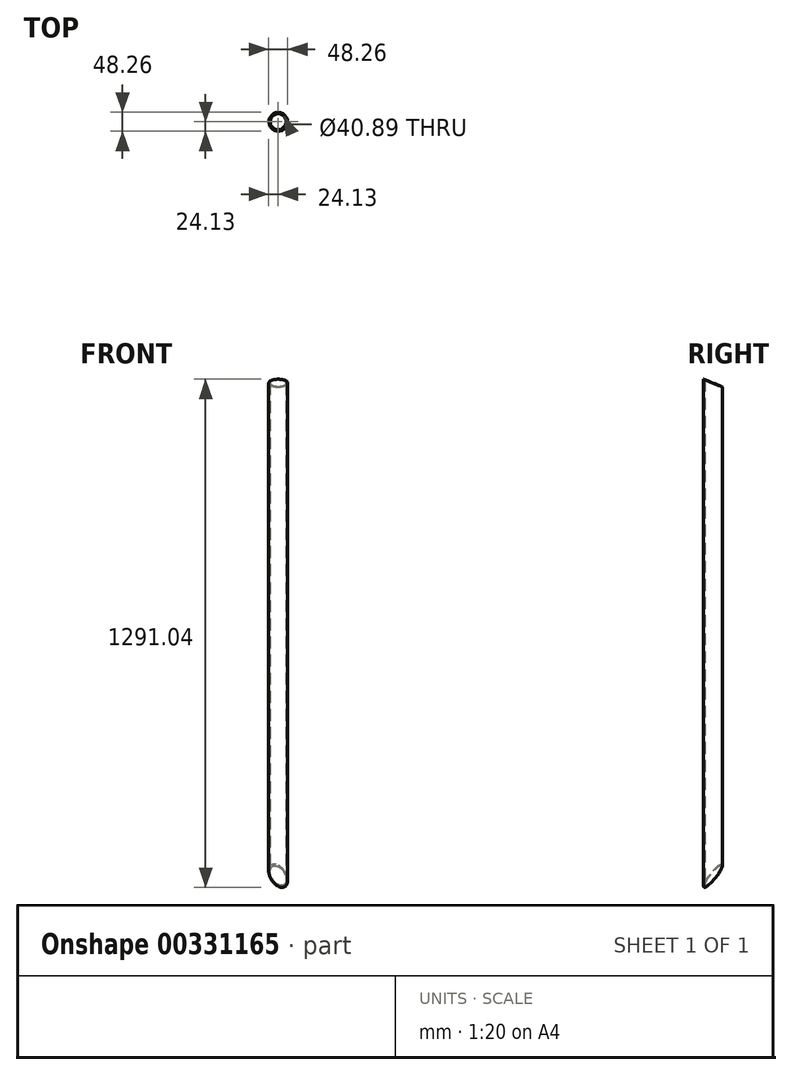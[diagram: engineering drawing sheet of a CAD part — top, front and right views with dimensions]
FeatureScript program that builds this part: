
annotation { "Feature Type Name" : "Feature", "Feature Type Description" : "" }
export const myFeature = defineFeature(function(context is Context, id is Id, definition is map)
    precondition{}
    {
        {
            var Q0;
            Q0=qCreatedBy(makeId("Top.planeOp"),FACE);
            var sketch = newSketch(context, id + "F0", { "sketchPlane" : qUnion([Q0])});
            skCircle(sketch, "E0", {"center": v(0, 0) * mm, "radius": 20.45 * mm});
            skCircle(sketch, "E1.0", {"center": v(0, 0) * mm, "radius": 24.13 * mm});
            skSolve(sketch);
        }
        {
            var Q0;
            Q0=qSketchRegion(id+"F0",true);
            extrude(context, id + "F1", {"entities" : qUnion([Q0]), "depth" : 1308.1 * mm});
        }
        {
            var Q0;
            Q0=qCreatedBy(makeId("Right.planeOp"),FACE);
            var sketch = newSketch(context, id + "F2", { "sketchPlane" : qUnion([Q0])});
            skLineSegment(sketch, "E2.bottom", {"start": v(24.13, 1308.1) * mm, "end": v(-24.13, 1308.1) * mm});
            skLineSegment(sketch, "E2.left", {"start": v(24.13, 1308.1) * mm, "end": v(24.13, 1288.36) * mm});
            skPoint(sketch, "E2.middle", {"position": v(0, 1298.23) * mm});
            skLineSegment(sketch, "E3", {"start": v(-24.13, 1308.1) * mm, "end": v(24.13, 1288.36) * mm});
            skPoint(sketch, "E2.top.end.orphan", {"position": v(-24.13, 1288.36) * mm});
            skSolve(sketch);
        }
        {
            var Q0;
            Q0=qSketchRegion(id+"F2",true);
            extrude(context, id + "F3", {"entities" : qUnion([Q0]), "operationType" : NewBodyOperationType.REMOVE, "endBound" : BoundingType.THROUGH_ALL, "oppositeDirection" : true, "depth" : 25.4 * mm, "hasSecondDirection" : true, "secondDirectionBound" : SecondDirectionBoundingType.THROUGH_ALL, "secondDirectionOppositeDirection" : false, "secondDirectionDepth" : 25.4 * mm});
        }
        {
            var Q0;
            Q0=qCreatedBy(makeId("Front.planeOp"),FACE);
            var sketch = newSketch(context, id + "F4", { "sketchPlane" : qUnion([Q0])});
            skLineSegment(sketch, "E4.top", {"start": v(28.58, 0) * mm, "end": v(-28.58, 0) * mm});
            skPoint(sketch, "E4.middle", {"position": v(0, 14.55) * mm});
            skPoint(sketch, "E4.right.start.orphan", {"position": v(-28.58, 29.1) * mm});
            skLineSegment(sketch, "E5", {"start": v(-28.58, 29.1) * mm, "end": v(-28.58, 0) * mm});
            skLineSegment(sketch, "E6", {"start": v(-28.57, 29.1) * mm, "end": v(28.57, 0) * mm});
            skPoint(sketch, "E4.left.start.orphan", {"position": v(28.58, 29.1) * mm});
            skSolve(sketch);
        }
        {
            var Q0;
            Q0=qSketchRegion(id+"F4",true);
            extrude(context, id + "F5", {"entities" : qUnion([Q0]), "operationType" : NewBodyOperationType.REMOVE, "endBound" : BoundingType.THROUGH_ALL, "depth" : 25.4 * mm, "hasSecondDirection" : true, "secondDirectionBound" : SecondDirectionBoundingType.THROUGH_ALL, "secondDirectionOppositeDirection" : true, "secondDirectionDepth" : 25.4 * mm});
        }
        {
            var Q0;
            Q0=makeQuery(id+"F5.boolean.opBoolean","COPY",FACE,{"derivedFrom":makeQuery(id+"F5.opExtrude","SWEPT_FACE",FACE,{"disambiguationData":[OSD([sQuery(id+"F4.wireOp",EDGE,"E6")])]})});
            var sketch = newSketch(context, id + "F6", { "sketchPlane" : qUnion([Q0])});
            skLineSegment(sketch, "E7", {"start": v(-29.55, 0) * mm, "end": v(16.34, 0) * mm});
            skSolve(sketch);
        }
        {
            var Q0;
            Q0=sQuery(id+"F6.wireOp",EDGE,"E7");
            cPlane(context, id + "F7", {"entities" : qUnion([Q0]), "cplaneType" : CPlaneType.LINE_ANGLE, "offset" : 25.4 * mm, "angle" : 45 * degree, "oppositeDirection" : true, "width" : 152.4 * mm, "height" : 152.4 * mm});
        }
        {
            var Q0;
            Q0=qCreatedBy(id+"F7.planeOp",FACE);
            var sketch = newSketch(context, id + "F8", { "sketchPlane" : qUnion([Q0])});
            skLineSegment(sketch, "E8.bottom", {"start": v(-83.87, 91.05) * mm, "end": v(94.55, 91.05) * mm});
            skLineSegment(sketch, "E8.top", {"start": v(-83.87, -76.34) * mm, "end": v(94.55, -76.34) * mm});
            skLineSegment(sketch, "E8.left", {"start": v(-83.87, 91.05) * mm, "end": v(-83.87, -76.34) * mm});
            skLineSegment(sketch, "E8.right", {"start": v(94.55, 91.05) * mm, "end": v(94.55, -76.34) * mm});
            skPoint(sketch, "E8.middle", {"position": v(5.34, 7.36) * mm});
            skSolve(sketch);
        }
        {
            var Q0;
            Q0 = qSketchRegion(id + "F8", true);
            extrude(context, id + "F9", {"entities" : qUnion([Q0]), "operationType" : NewBodyOperationType.REMOVE, "depth" : 50.8 * mm, "hasSecondDirection" : true, "secondDirectionOppositeDirection" : true, "secondDirectionDepth" : 20.32 * mm});
        }
    });
